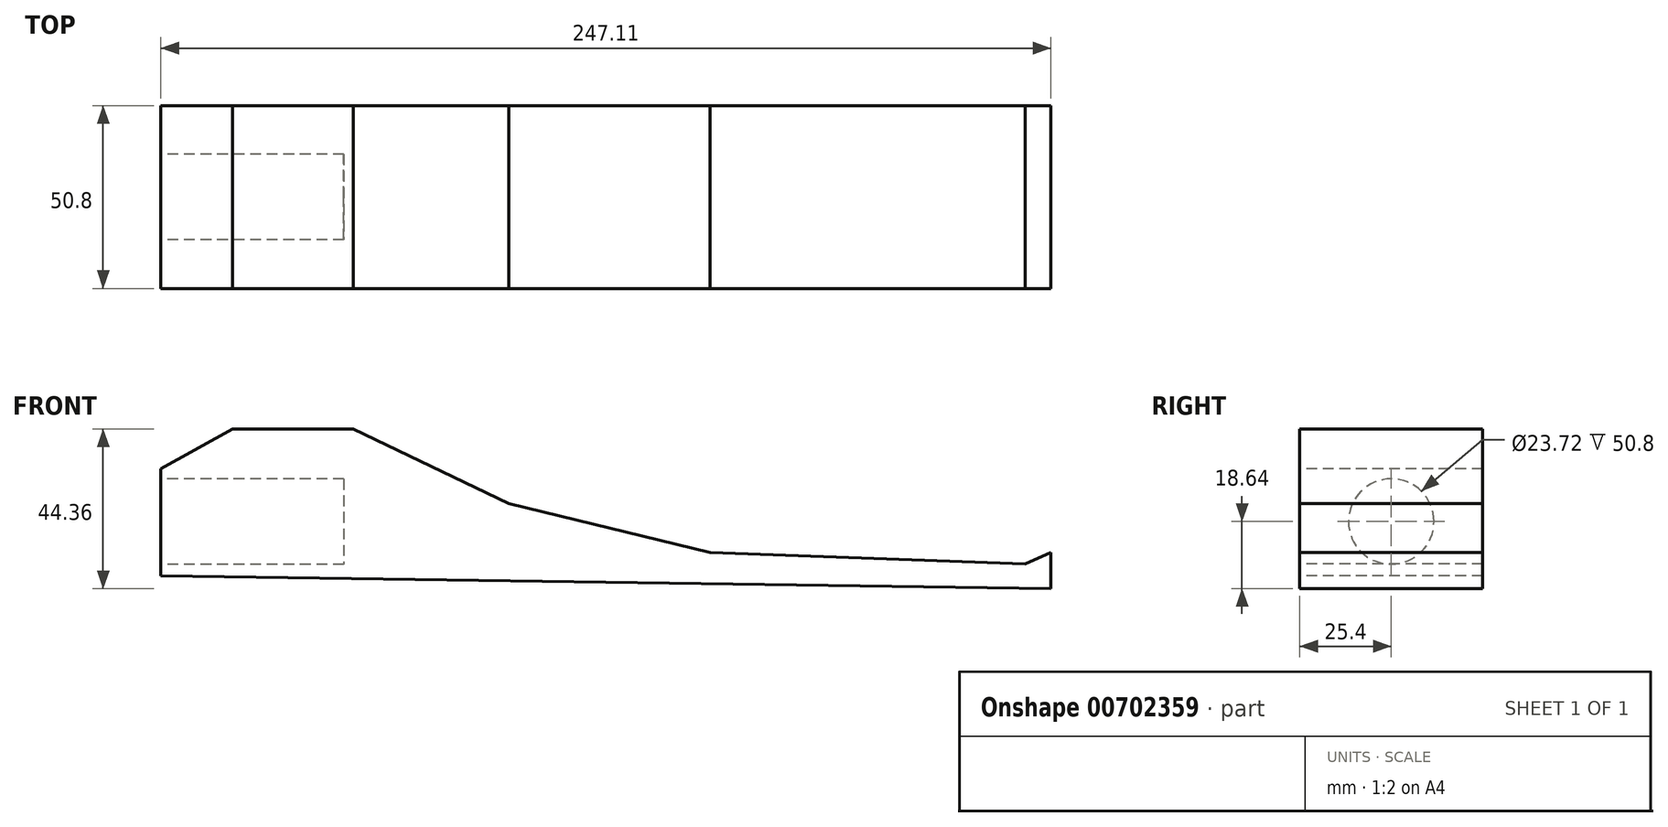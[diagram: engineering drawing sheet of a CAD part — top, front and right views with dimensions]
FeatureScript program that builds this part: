
annotation { "Feature Type Name" : "Feature", "Feature Type Description" : "" }
export const myFeature = defineFeature(function(context is Context, id is Id, definition is map)
    precondition{}
    {
        {
            var Q0;
            Q0=qCreatedBy(makeId("Front.planeOp"),FACE);
            var sketch = newSketch(context, id + "F0", { "sketchPlane" : qUnion([Q0])});
            skLineSegment(sketch, "E0", {"start": v(0, 0) * mm, "end": v(304.8, 0) * mm});
            skLineSegment(sketch, "E1", {"start": v(0, 0) * mm, "end": v(0, 63.13) * mm});
            skLineSegment(sketch, "E2", {"start": v(304.8, 0) * mm, "end": v(304.8, 17.08) * mm});
            skLineSegment(sketch, "E3", {"start": v(304.8, 17.08) * mm, "end": v(0, 63.13) * mm});
            skSolve(sketch);
        }
        {
            var Q0;
            Q0 = qSketchRegion(id + "F0", true);
            extrude(context, id + "F1", {"entities" : qUnion([Q0]), "depth" : 50.8 * mm, "offsetDistance" : 25.4 * mm});
        }
        {
            var Q0;
            Q0=makeQuery(id+"F1.opExtrude","SWEPT_FACE",FACE,{"disambiguationData":[OSD([sQuery(id+"F0.wireOp",EDGE,"E1")])]});
            var sketch = newSketch(context, id + "F2", { "sketchPlane" : qUnion([Q0])});
            skCircle(sketch, "E4", {"center": v(25.4, 25.63) * mm, "radius": 11.86 * mm});
            skPoint(sketch, "E4.centerSnap0", {"position": v(25.4, 0) * mm});
            skSolve(sketch);
        }
        {
            var Q0;
            Q0=makeQuery(id+"F1.opExtrude","CAP_FACE",FACE,{"disambiguationData":[OSD([sQuery(id+"F0.wireOp",EDGE,"E0"),sQuery(id+"F0.wireOp",EDGE,"E1"),sQuery(id+"F0.wireOp",EDGE,"E2"),sQuery(id+"F0.wireOp",EDGE,"E3")])],"isStart":false});
            var sketch = newSketch(context, id + "F3", { "sketchPlane" : qUnion([Q0])});
            skLineSegment(sketch, "E5", {"start": v(0, 40.27) * mm, "end": v(19.83, 51.35) * mm});
            skLineSegment(sketch, "E6", {"start": v(19.83, 51.35) * mm, "end": v(53.36, 51.35) * mm});
            skLineSegment(sketch, "E7", {"start": v(53.36, 51.35) * mm, "end": v(96.56, 30.65) * mm});
            skLineSegment(sketch, "E8", {"start": v(96.56, 30.65) * mm, "end": v(152.48, 17.08) * mm});
            skLineSegment(sketch, "E9", {"start": v(152.48, 17.08) * mm, "end": v(239.94, 13.8) * mm});
            skLineSegment(sketch, "E10", {"start": v(0, 10.57) * mm, "end": v(247.11, 7) * mm});
            skLineSegment(sketch, "E11", {"start": v(247.11, 7) * mm, "end": v(247.11, 17.03) * mm});
            skLineSegment(sketch, "E12", {"start": v(247.11, 17.03) * mm, "end": v(239.94, 13.8) * mm});
            skSolve(sketch);
        }
        {
            var Q0;
            Q0 = qSketchRegion(id + "F2", true);
            extrude(context, id + "F4", {"entities" : qUnion([Q0]), "operationType" : NewBodyOperationType.REMOVE, "oppositeDirection" : true, "depth" : 50.8 * mm, "offsetDistance" : 25.4 * mm});
        }
        {
            var Q0;
            {var subQ2=sQuery(id+"F3.wireOp",EDGE,"E5");Q0=makeQuery(id+"F3.imprint","IMPRINT",FACE,{"disambiguationData":[TD([[makeQuery(id+"F3.imprint","IMPRINT",EDGE,{"derivedFrom":subQ2}),1.0]])]});}
            extrude(context, id + "F5", {"entities" : qUnion([Q0]), "operationType" : NewBodyOperationType.REMOVE, "oppositeDirection" : true, "depth" : 76.2 * mm, "offsetDistance" : 25.4 * mm});
        }
    });
